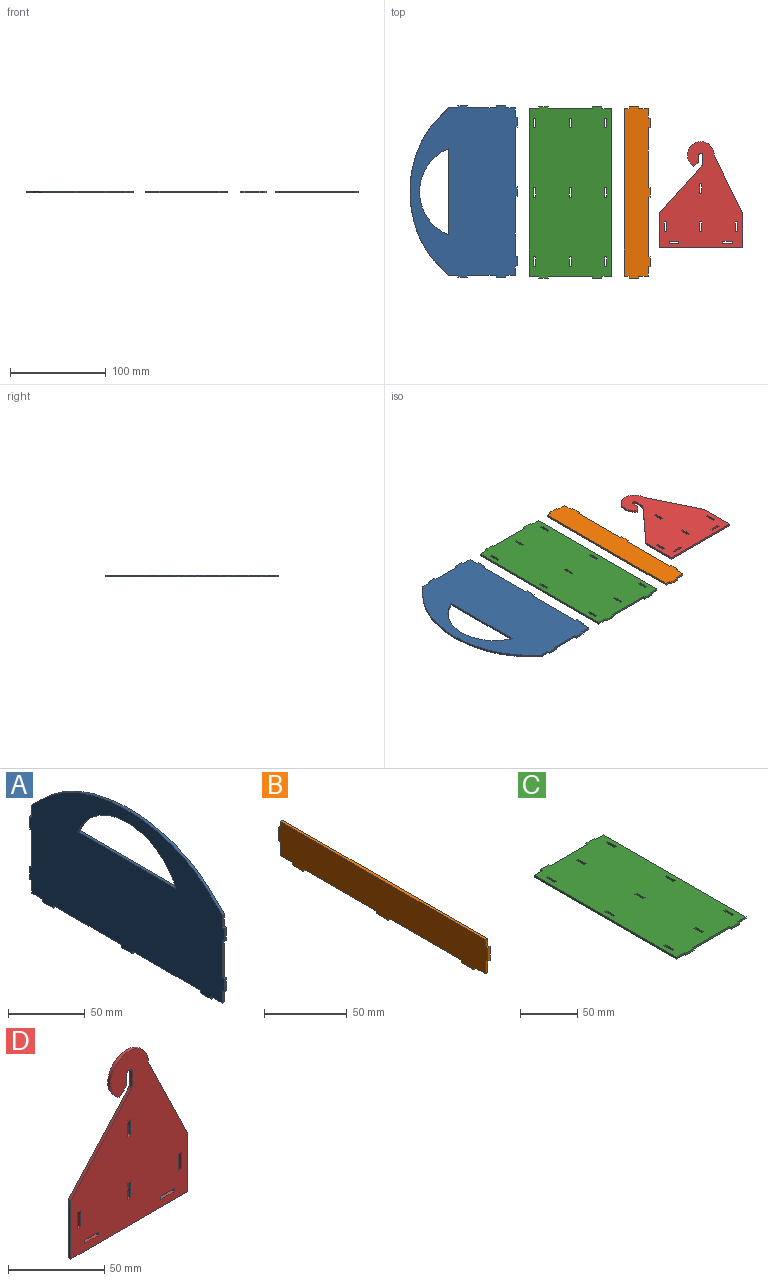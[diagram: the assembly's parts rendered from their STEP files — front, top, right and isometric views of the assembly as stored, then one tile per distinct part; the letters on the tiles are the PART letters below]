
ASSEMBLY  parts=4 mates=3
PART A: 37 faces, bbox 2x179x112 mm
  f0: plane 62.5x2mm, normal (0,0,-1), area 125mm2, adj f8,f10,f30,f35
  f1: plane 62.5x2mm, normal (0,0,-1), area 125mm2, adj f8,f10,f33,f36
  f2: plane 10x2mm, normal (0,0,-1), area 20mm2, adj f5,f8,f10,f29
  f3: plane 10x2mm, normal (0,1,0), area 20mm2, adj f8,f9,f10,f27
  f4: plane 30x2mm, normal (0,1,0), area 60mm2, adj f8,f10,f24,f26
  f5: plane 10x2mm, normal (0,-1,0), area 20mm2, adj f2,f8,f10,f21
  f6: plane 30x2mm, normal (0,-1,0), area 60mm2, adj f8,f10,f18,f20
  f7: plane 90x2mm, normal (0,0,1), area 180mm2, adj f8,f10,f14
  f8: plane 179x112mm, normal (-1,0,0), area 15314.4mm2, adj f0,f1,f2,f3,f4,f5,f6,f7
  f9: plane 10x2mm, normal (0,0,-1), area 20mm2, adj f3,f8,f10,f32
  f10: plane 179x112mm, normal (1,0,0), area 15314.4mm2, adj f0,f1,f2,f3,f4,f5,f6,f7
  f11: plane 10x2mm, normal (0,1,0), area 20mm2, adj f8,f10,f13,f23
  f12: plane 10x2mm, normal (0,-1,0), area 20mm2, adj f8,f10,f15,f17
  f13: extruded ~87.5x40mm, area 198.6mm2, adj f8,f10,f11,f15
  f14: cylinder r=48.75mm len=90mm, axis (1,0,0), area 229.3mm2, adj f7,f8,f10
  f15: extruded ~87.5x40mm, area 198.6mm2, adj f8,f10,f12,f13
  f16: plane 10x2mm, normal (0,-1,0), area 20mm2, adj f8,f10,f17,f18
  f17: plane 2x2mm, normal (0,0,1), area 4mm2, adj f8,f10,f12,f16
  f18: plane 2x2mm, normal (0,0,-1), area 4mm2, adj f6,f8,f10,f16
  f19: plane 10x2mm, normal (0,-1,0), area 20mm2, adj f8,f10,f20,f21
  f20: plane 2x2mm, normal (0,0,1), area 4mm2, adj f6,f8,f10,f19
  f21: plane 2x2mm, normal (0,0,-1), area 4mm2, adj f5,f8,f10,f19
  f22: plane 10x2mm, normal (0,1,0), area 20mm2, adj f8,f10,f23,f24
  f23: plane 2x2mm, normal (0,0,1), area 4mm2, adj f8,f10,f11,f22
  f24: plane 2x2mm, normal (0,0,-1), area 4mm2, adj f4,f8,f10,f22
  f25: plane 10x2mm, normal (0,1,0), area 20mm2, adj f8,f10,f26,f27
  f26: plane 2x2mm, normal (0,0,1), area 4mm2, adj f4,f8,f10,f25
  f27: plane 2x2mm, normal (0,0,-1), area 4mm2, adj f3,f8,f10,f25
  f28: plane 10x2mm, normal (0,0,-1), area 20mm2, adj f8,f10,f29,f30
  f29: plane 2x2mm, normal (0,-1,0), area 4mm2, adj f2,f8,f10,f28
  f30: plane 2x2mm, normal (0,1,0), area 4mm2, adj f0,f8,f10,f28
  f31: plane 10x2mm, normal (0,0,-1), area 20mm2, adj f8,f10,f32,f33
  f32: plane 2x2mm, normal (0,1,0), area 4mm2, adj f8,f9,f10,f31
  f33: plane 2x2mm, normal (0,-1,0), area 4mm2, adj f1,f8,f10,f31
  f34: plane 10x2mm, normal (0,0,-1), area 20mm2, adj f8,f10,f35,f36
  f35: plane 2x2mm, normal (0,-1,0), area 4mm2, adj f0,f8,f10,f34
  f36: plane 2x2mm, normal (0,1,0), area 4mm2, adj f1,f8,f10,f34
PART B: 26 faces, bbox 2x179x27 mm
  f0: plane 62.5x2mm, normal (0,0,-1), area 125mm2, adj f5,f7,f19,f24
  f1: plane 62.5x2mm, normal (0,0,-1), area 125mm2, adj f5,f7,f22,f25
  f2: plane 10x2mm, normal (0,0,-1), area 20mm2, adj f4,f5,f7,f18
  f3: plane 10x2mm, normal (0,1,0), area 20mm2, adj f5,f6,f7,f16
  f4: plane 10x2mm, normal (0,-1,0), area 20mm2, adj f2,f5,f7,f13
  f5: plane 179x27mm, normal (-1,0,0), area 4475mm2, adj f0,f1,f2,f3,f4,f6,f8,f9
  f6: plane 10x2mm, normal (0,0,-1), area 20mm2, adj f3,f5,f7,f21
  f7: plane 179x27mm, normal (1,0,0), area 4475mm2, adj f0,f1,f2,f3,f4,f6,f8,f9
  f8: plane 175x2mm, normal (0,0,1), area 350mm2, adj f5,f7,f9,f10
  f9: plane 5x2mm, normal (0,1,0), area 10mm2, adj f5,f7,f8,f15
  f10: plane 5x2mm, normal (0,-1,0), area 10mm2, adj f5,f7,f8,f12
  f11: plane 10x2mm, normal (0,-1,0), area 20mm2, adj f5,f7,f12,f13
  f12: plane 2x2mm, normal (0,0,1), area 4mm2, adj f5,f7,f10,f11
  f13: plane 2x2mm, normal (0,0,-1), area 4mm2, adj f4,f5,f7,f11
  f14: plane 10x2mm, normal (0,1,0), area 20mm2, adj f5,f7,f15,f16
  f15: plane 2x2mm, normal (0,0,1), area 4mm2, adj f5,f7,f9,f14
  f16: plane 2x2mm, normal (0,0,-1), area 4mm2, adj f3,f5,f7,f14
  f17: plane 10x2mm, normal (0,0,-1), area 20mm2, adj f5,f7,f18,f19
  f18: plane 2x2mm, normal (0,-1,0), area 4mm2, adj f2,f5,f7,f17
  f19: plane 2x2mm, normal (0,1,0), area 4mm2, adj f0,f5,f7,f17
  f20: plane 10x2mm, normal (0,0,-1), area 20mm2, adj f5,f7,f21,f22
  f21: plane 2x2mm, normal (0,1,0), area 4mm2, adj f5,f6,f7,f20
  f22: plane 2x2mm, normal (0,-1,0), area 4mm2, adj f1,f5,f7,f20
  f23: plane 10x2mm, normal (0,0,-1), area 20mm2, adj f5,f7,f24,f25
  f24: plane 2x2mm, normal (0,-1,0), area 4mm2, adj f0,f5,f7,f23
  f25: plane 2x2mm, normal (0,1,0), area 4mm2, adj f1,f5,f7,f23
PART C: 58 faces, bbox 86x179x2 mm
  f0: plane 179x86mm, normal (0,0,1), area 14928mm2, adj f2,f3,f4,f5,f6,f7,f8,f9
  f1: plane 179x86mm, normal (0,0,-1), area 14928mm2, adj f2,f3,f4,f5,f6,f7,f8,f9
  f2: plane 46x2mm, normal (0,1,0), area 92mm2, adj f0,f1,f18,f21
  f3: plane 10x2mm, normal (0,1,0), area 20mm2, adj f0,f1,f7,f17
  f4: plane 46x2mm, normal (0,-1,0), area 92mm2, adj f0,f1,f11,f15
  f5: plane 10x2mm, normal (0,-1,0), area 20mm2, adj f0,f1,f7,f12
  f6: plane 175x2mm, normal (-1,0,0), area 350mm2, adj f0,f1,f8,f9
  f7: plane 175x2mm, normal (1,0,0), area 350mm2, adj f0,f1,f3,f5
  f8: plane 10x2mm, normal (0,-1,0), area 20mm2, adj f0,f1,f6,f14
  f9: plane 10x2mm, normal (0,1,0), area 20mm2, adj f0,f1,f6,f20
  f10: plane 10x2mm, normal (0,-1,0), area 20mm2, adj f0,f1,f11,f12
  f11: plane 2x2mm, normal (-1,0,0), area 4mm2, adj f0,f1,f4,f10
  f12: plane 2x2mm, normal (1,0,0), area 4mm2, adj f0,f1,f5,f10
  f13: plane 10x2mm, normal (0,-1,0), area 20mm2, adj f0,f1,f14,f15
  f14: plane 2x2mm, normal (-1,0,0), area 4mm2, adj f0,f1,f8,f13
  f15: plane 2x2mm, normal (1,0,0), area 4mm2, adj f0,f1,f4,f13
  f16: plane 10x2mm, normal (0,1,0), area 20mm2, adj f0,f1,f17,f18
  f17: plane 2x2mm, normal (1,0,0), area 4mm2, adj f0,f1,f3,f16
  f18: plane 2x2mm, normal (-1,0,0), area 4mm2, adj f0,f1,f2,f16
  f19: plane 10x2mm, normal (0,1,0), area 20mm2, adj f0,f1,f20,f21
  f20: plane 2x2mm, normal (-1,0,0), area 4mm2, adj f0,f1,f9,f19
  f21: plane 2x2mm, normal (1,0,0), area 4mm2, adj f0,f1,f2,f19
  f22: plane 10.2x2mm, normal (1,0,0), area 20.4mm2, adj f0,f1,f23,f24
  f23: plane 2.2x2mm, normal (0,1,0), area 4.4mm2, adj f0,f1,f22,f25
  f24: plane 2.2x2mm, normal (0,-1,0), area 4.4mm2, adj f0,f1,f22,f25
  f25: plane 10.2x2mm, normal (-1,0,0), area 20.4mm2, adj f0,f1,f23,f24
  f26: plane 2.2x2mm, normal (0,-1,0), area 4.4mm2, adj f0,f1,f27,f28
  f27: plane 10.2x2mm, normal (1,0,0), area 20.4mm2, adj f0,f1,f26,f29
  f28: plane 10.2x2mm, normal (-1,0,0), area 20.4mm2, adj f0,f1,f26,f29
  f29: plane 2.2x2mm, normal (0,1,0), area 4.4mm2, adj f0,f1,f27,f28
  f30: plane 10.2x2mm, normal (-1,0,0), area 20.4mm2, adj f0,f1,f31,f33
  f31: plane 2.2x2mm, normal (0,1,0), area 4.4mm2, adj f0,f1,f30,f32
  f32: plane 10.2x2mm, normal (1,0,0), area 20.4mm2, adj f0,f1,f31,f33
  f33: plane 2.2x2mm, normal (0,-1,0), area 4.4mm2, adj f0,f1,f30,f32
  f34: plane 10.2x2mm, normal (-1,0,0), area 20.4mm2, adj f0,f1,f35,f37
  f35: plane 2.2x2mm, normal (0,1,0), area 4.4mm2, adj f0,f1,f34,f36
  f36: plane 10.2x2mm, normal (1,0,0), area 20.4mm2, adj f0,f1,f35,f37
  f37: plane 2.2x2mm, normal (0,-1,0), area 4.4mm2, adj f0,f1,f34,f36
  f38: plane 10.2x2mm, normal (1,0,0), area 20.4mm2, adj f0,f1,f39,f40
  f39: plane 2.2x2mm, normal (0,1,0), area 4.4mm2, adj f0,f1,f38,f41
  f40: plane 2.2x2mm, normal (0,-1,0), area 4.4mm2, adj f0,f1,f38,f41
  f41: plane 10.2x2mm, normal (-1,0,0), area 20.4mm2, adj f0,f1,f39,f40
  f42: plane 10.2x2mm, normal (1,0,0), area 20.4mm2, adj f0,f1,f43,f44
  f43: plane 2.2x2mm, normal (0,1,0), area 4.4mm2, adj f0,f1,f42,f45
  f44: plane 2.2x2mm, normal (0,-1,0), area 4.4mm2, adj f0,f1,f42,f45
  f45: plane 10.2x2mm, normal (-1,0,0), area 20.4mm2, adj f0,f1,f43,f44
  f46: plane 2.2x2mm, normal (0,-1,0), area 4.4mm2, adj f0,f1,f47,f49
  f47: plane 10.2x2mm, normal (-1,0,0), area 20.4mm2, adj f0,f1,f46,f48
  f48: plane 2.2x2mm, normal (0,1,0), area 4.4mm2, adj f0,f1,f47,f49
  f49: plane 10.2x2mm, normal (1,0,0), area 20.4mm2, adj f0,f1,f46,f48
  f50: plane 10.2x2mm, normal (1,0,0), area 20.4mm2, adj f0,f1,f51,f52
  f51: plane 2.2x2mm, normal (0,1,0), area 4.4mm2, adj f0,f1,f50,f53
  f52: plane 2.2x2mm, normal (0,-1,0), area 4.4mm2, adj f0,f1,f50,f53
  f53: plane 10.2x2mm, normal (-1,0,0), area 20.4mm2, adj f0,f1,f51,f52
  f54: plane 2.2x2mm, normal (0,-1,0), area 4.4mm2, adj f0,f1,f55,f57
  f55: plane 10.2x2mm, normal (-1,0,0), area 20.4mm2, adj f0,f1,f54,f56
  f56: plane 2.2x2mm, normal (0,1,0), area 4.4mm2, adj f0,f1,f55,f57
  f57: plane 10.2x2mm, normal (1,0,0), area 20.4mm2, adj f0,f1,f54,f56
PART D: 39 faces, bbox 86x2x111 mm
  f0: plane 111x86mm, normal (0,-1,0), area 6158.2mm2, adj f2,f3,f4,f5,f6,f7,f8,f9
  f1: plane 111x86mm, normal (0,1,0), area 6158.2mm2, adj f2,f3,f4,f5,f6,f7,f8,f9
  f2: cylinder r=14mm len=28mm, axis (0,1,0), area 116.2mm2, adj f0,f1,f3,f14
  f3: plane 3.59x3.01mm, normal (0.64,0,-0.77), area 9.4mm2, adj f0,f1,f2,f4
  f4: cylinder r=5mm len=3.83mm, axis (0,1,0), area 8.7mm2, adj f0,f1,f3,f5
  f5: plane 5x2mm, normal (1,0,0), area 10mm2, adj f0,f1,f4,f6
  f6: cylinder r=2.1mm len=4.2mm, axis (0,1,0), area 13.2mm2, adj f0,f1,f5,f7
  f7: plane 8.22x2mm, normal (-1,0,0), area 16.4mm2, adj f0,f1,f6,f8
  f8: cylinder r=5mm len=3.21mm, axis (0,1,0), area 7mm2, adj f0,f1,f7,f9
  f9: plane 2.51x2.11mm, normal (-0.77,0,0.64), area 6.6mm2, adj f0,f1,f8,f10
  f10: plane 46.05x41.82mm, normal (-0.74,0,0.67), area 124.4mm2, adj f0,f1,f9,f11
  f11: plane 37x2mm, normal (-1,0,0), area 74mm2, adj f0,f1,f10,f12
  f12: plane 86x2mm, normal (0,0,-1), area 172mm2, adj f0,f1,f11,f13
  f13: plane 37x2mm, normal (1,0,0), area 74mm2, adj f0,f1,f12,f14
  f14: plane 60x29mm, normal (0.9,0,0.44), area 133.3mm2, adj f0,f1,f2,f13
  f15: plane 2.2x2mm, normal (0,0,-1), area 4.4mm2, adj f0,f1,f16,f18
  f16: plane 10.2x2mm, normal (1,0,0), area 20.4mm2, adj f0,f1,f15,f17
  f17: plane 2.2x2mm, normal (0,0,1), area 4.4mm2, adj f0,f1,f16,f18
  f18: plane 10.2x2mm, normal (-1,0,0), area 20.4mm2, adj f0,f1,f15,f17
  f19: plane 2.2x2mm, normal (1,0,0), area 4.4mm2, adj f0,f1,f20,f21
  f20: plane 10.2x2mm, normal (0,0,-1), area 20.4mm2, adj f0,f1,f19,f22
  f21: plane 10.2x2mm, normal (0,0,1), area 20.4mm2, adj f0,f1,f19,f22
  f22: plane 2.2x2mm, normal (-1,0,0), area 4.4mm2, adj f0,f1,f20,f21
  f23: plane 10.2x2mm, normal (0,0,1), area 20.4mm2, adj f0,f1,f24,f26
  f24: plane 2.2x2mm, normal (-1,0,0), area 4.4mm2, adj f0,f1,f23,f25
  f25: plane 10.2x2mm, normal (0,0,-1), area 20.4mm2, adj f0,f1,f24,f26
  f26: plane 2.2x2mm, normal (1,0,0), area 4.4mm2, adj f0,f1,f23,f25
  f27: plane 10.2x2mm, normal (1,0,0), area 20.4mm2, adj f0,f1,f28,f30
  f28: plane 2.2x2mm, normal (0,0,1), area 4.4mm2, adj f0,f1,f27,f29
  f29: plane 10.2x2mm, normal (-1,0,0), area 20.4mm2, adj f0,f1,f28,f30
  f30: plane 2.2x2mm, normal (0,0,-1), area 4.4mm2, adj f0,f1,f27,f29
  f31: plane 2.2x2mm, normal (0,0,1), area 4.4mm2, adj f0,f1,f32,f34
  f32: plane 10.2x2mm, normal (-1,0,0), area 20.4mm2, adj f0,f1,f31,f33
  f33: plane 2.2x2mm, normal (0,0,-1), area 4.4mm2, adj f0,f1,f32,f34
  f34: plane 10.2x2mm, normal (1,0,0), area 20.4mm2, adj f0,f1,f31,f33
  f35: plane 2.2x2mm, normal (0,0,-1), area 4.4mm2, adj f0,f1,f36,f38
  f36: plane 10.2x2mm, normal (1,0,0), area 20.4mm2, adj f0,f1,f35,f37
  f37: plane 2.2x2mm, normal (0,0,1), area 4.4mm2, adj f0,f1,f36,f38
  f38: plane 10.2x2mm, normal (-1,0,0), area 20.4mm2, adj f0,f1,f35,f37
PLACE A rot(axis=(0,-1,0),90deg) t=(108.57,93.84,40.68)mm
PLACE B rot(axis=(0,-1,0),90deg) t=(247.44,93.2,3.68)mm
PLACE C t=(165.98,93.2,41.68)mm
PLACE D rot(axis=(-1,0,0),90deg) t=(302.3,42.11,-47.82)mm
MATE planar B.f5 <-> C.f1  axis (0,0,-1) through (235.09,93.2,39.68)mm
MATE planar C.f1 <-> A.f8  axis (0,0,-1) through (164.88,93.2,39.68)mm
MATE planar D.f1 <-> C.f1  axis (0,0,-1) through (304.1,76.35,39.68)mm
